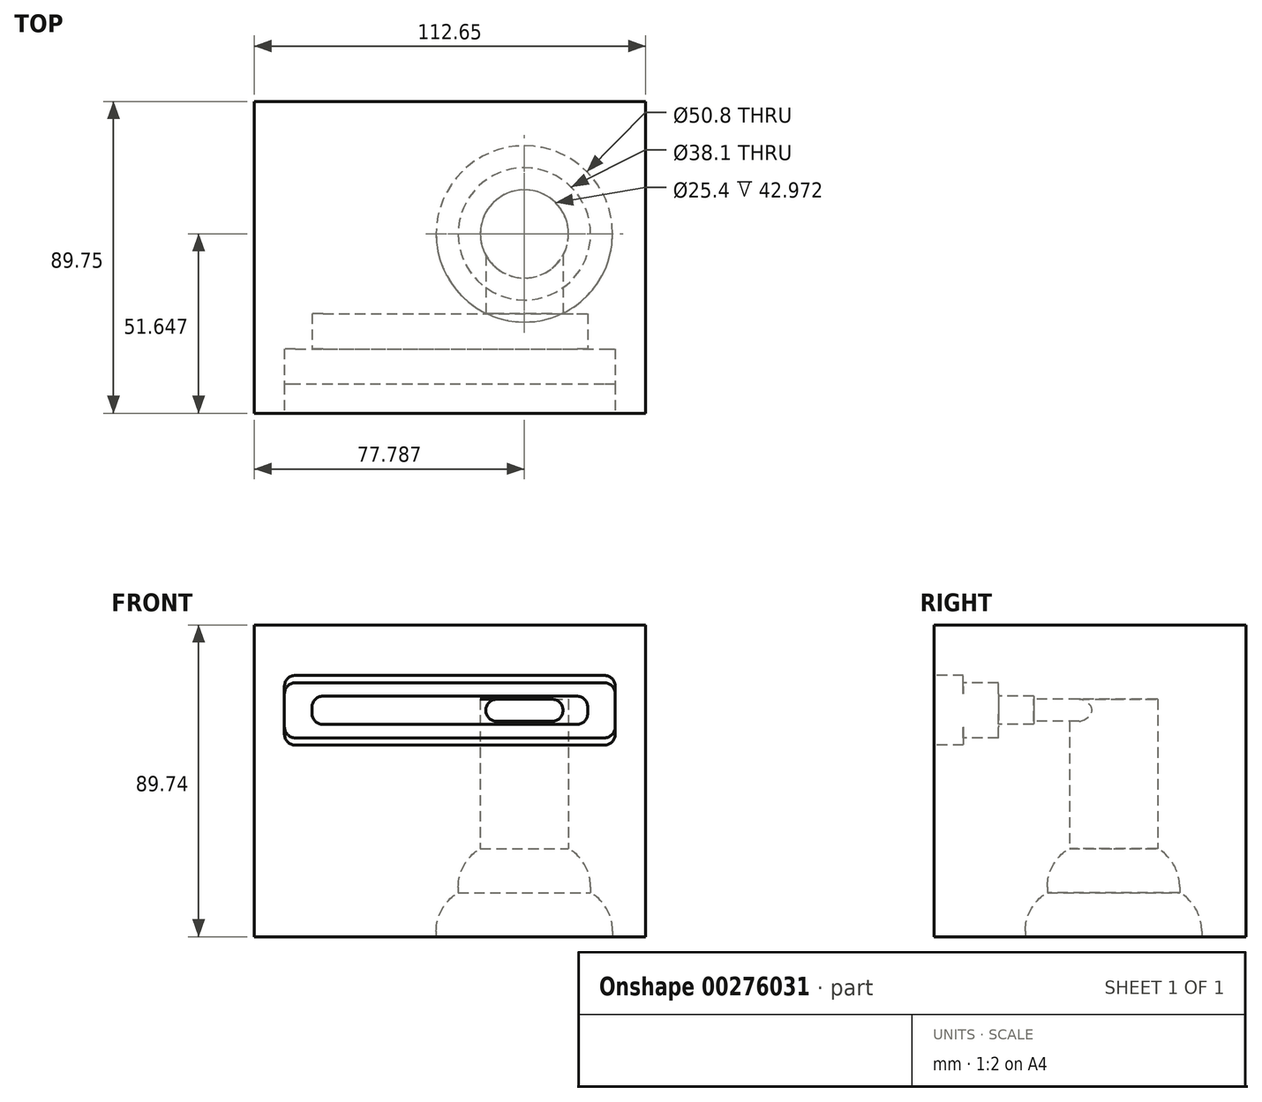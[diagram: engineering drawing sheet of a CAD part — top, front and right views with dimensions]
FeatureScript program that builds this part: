
annotation { "Feature Type Name" : "Feature", "Feature Type Description" : "" }
export const myFeature = defineFeature(function(context is Context, id is Id, definition is map)
    precondition{}
    {
        {
            var Q0;
            Q0=qCreatedBy(makeId("Right.planeOp"),FACE);
            var sketch = newSketch(context, id + "F0", { "sketchPlane" : qUnion([Q0])});
            skLineSegment(sketch, "E0.bottom", {"start": v(-45.07, 37.37) * mm, "end": v(44.68, 37.37) * mm});
            skLineSegment(sketch, "E0.top", {"start": v(-45.07, -52.37) * mm, "end": v(44.68, -52.37) * mm});
            skLineSegment(sketch, "E0.left", {"start": v(-45.07, 37.37) * mm, "end": v(-45.07, -52.37) * mm});
            skLineSegment(sketch, "E0.right", {"start": v(44.68, 37.37) * mm, "end": v(44.68, -52.37) * mm});
            skSolve(sketch);
        }
        {
            var Q0;
            Q0 = qSketchRegion(id + "F0", true);
            extrude(context, id + "F1", {"entities" : qUnion([Q0]), "depth" : 112.65 * mm});
        }
        {
            var Q0;
            Q0=makeQuery(id+"F1.opExtrude","SWEPT_FACE",FACE,{"disambiguationData":[OSD([sQuery(id+"F0.wireOp",EDGE,"E0.left")])]});
            var sketch = newSketch(context, id + "F2", { "sketchPlane" : qUnion([Q0])});
            skLineSegment(sketch, "E1.0", {"start": v(100.77, 22.88) * mm, "end": v(11.87, 22.88) * mm});
            skLineSegment(sketch, "E2.0", {"start": v(100.77, 2.77) * mm, "end": v(11.87, 2.77) * mm});
            skLineSegment(sketch, "E3.0", {"start": v(8.7, 19.7) * mm, "end": v(8.7, 5.94) * mm});
            skLineSegment(sketch, "E4.0", {"start": v(103.95, 19.7) * mm, "end": v(103.95, 5.94) * mm});
            skLineSegment(sketch, "E5.3", {"start": v(-47.62, -100) * mm, "end": v(160.27, -100) * mm});
            skPoint(sketch, "E6.orphan", {"position": v(56.32, 37.37) * mm});
            skPoint(sketch, "E7.orphan", {"position": v(0, 12.83) * mm});
            skPoint(sketch, "E8.orphan", {"position": v(0, -7.5) * mm});
            skPoint(sketch, "E9.orphan", {"position": v(56.32, -52.37) * mm});
            skPoint(sketch, "E10.end.orphan", {"position": v(112.65, -7.5) * mm});
            skPoint(sketch, "E11.visualSharp", {"position": v(8.7, 22.88) * mm});
            skArc(sketch, "E11.filletArc", {"start": v(11.87, 22.88) * mm, "mid": v(9.63, 21.95) * mm, "end": v(8.7, 19.7) * mm});
            skPoint(sketch, "E12.visualSharp", {"position": v(8.7, 2.77) * mm});
            skArc(sketch, "E12.filletArc", {"start": v(8.7, 5.94) * mm, "mid": v(9.63, 3.7) * mm, "end": v(11.87, 2.77) * mm});
            skPoint(sketch, "E13.visualSharp", {"position": v(103.95, 2.77) * mm});
            skArc(sketch, "E13.filletArc", {"start": v(100.77, 2.77) * mm, "mid": v(103.02, 3.7) * mm, "end": v(103.95, 5.94) * mm});
            skPoint(sketch, "E14.visualSharp", {"position": v(103.95, 22.88) * mm});
            skArc(sketch, "E14.filletArc", {"start": v(103.95, 19.7) * mm, "mid": v(103.02, 21.95) * mm, "end": v(100.77, 22.88) * mm});
            skSolve(sketch);
        }
        {
            var Q0;
            Q0 = qSketchRegion(id + "F2", true);
            extrude(context, id + "F3", {"entities" : qUnion([Q0]), "operationType" : NewBodyOperationType.REMOVE, "oppositeDirection" : true, "depth" : 8.38 * mm});
        }
        {
            var Q0;
            Q0=makeQuery(id+"F3.boolean.opBoolean","COPY",FACE,{"derivedFrom":makeQuery(id+"F3.opExtrude","CAP_FACE",FACE,{"disambiguationData":[OSD([sQuery(id+"F2.wireOp",EDGE,"E1.0"),sQuery(id+"F2.wireOp",EDGE,"E2.0"),sQuery(id+"F2.wireOp",EDGE,"E3.0"),sQuery(id+"F2.wireOp",EDGE,"E4.0"),sQuery(id+"F2.wireOp",EDGE,"E11.filletArc"),sQuery(id+"F2.wireOp",EDGE,"E12.filletArc"),sQuery(id+"F2.wireOp",EDGE,"E13.filletArc"),sQuery(id+"F2.wireOp",EDGE,"E14.filletArc")])],"isStart":false})});
            var sketch = newSketch(context, id + "F4", { "sketchPlane" : qUnion([Q0])});
            skLineSegment(sketch, "E15.0", {"start": v(11.87, 4.89) * mm, "end": v(100.77, 4.89) * mm});
            skLineSegment(sketch, "E16.0", {"start": v(11.87, 20.76) * mm, "end": v(100.77, 20.76) * mm});
            skLineSegment(sketch, "E17", {"start": v(8.7, 17.59) * mm, "end": v(8.7, 8.06) * mm});
            skLineSegment(sketch, "E18", {"start": v(103.95, 17.59) * mm, "end": v(103.95, 8.06) * mm});
            skPoint(sketch, "E19.visualSharp", {"position": v(103.95, 20.76) * mm});
            skArc(sketch, "E19.filletArc", {"start": v(103.95, 17.59) * mm, "mid": v(103.02, 19.83) * mm, "end": v(100.77, 20.76) * mm});
            skPoint(sketch, "E20.visualSharp", {"position": v(103.95, 4.89) * mm});
            skArc(sketch, "E20.filletArc", {"start": v(100.77, 4.89) * mm, "mid": v(103.02, 5.82) * mm, "end": v(103.95, 8.06) * mm});
            skPoint(sketch, "E21.visualSharp", {"position": v(8.7, 4.89) * mm});
            skArc(sketch, "E21.filletArc", {"start": v(8.7, 8.06) * mm, "mid": v(9.63, 5.82) * mm, "end": v(11.87, 4.89) * mm});
            skPoint(sketch, "E22.visualSharp", {"position": v(8.7, 20.76) * mm});
            skArc(sketch, "E22.filletArc", {"start": v(11.87, 20.76) * mm, "mid": v(9.63, 19.83) * mm, "end": v(8.7, 17.59) * mm});
            skSolve(sketch);
        }
        {
            var Q0;
            Q0=makeQuery(id+"F4.imprint","IMPRINT",FACE,{"disambiguationData":[TD([[makeQuery(id+"F4.imprint","IMPRINT",EDGE,{"derivedFrom":sQuery(id+"F4.wireOp",EDGE,"E15.0")}),1.0]])]});
            extrude(context, id + "F5", {"entities" : qUnion([Q0]), "operationType" : NewBodyOperationType.REMOVE, "oppositeDirection" : true, "depth" : 10.16 * mm});
        }
        {
            var Q0;
            Q0=makeQuery(id+"F5.boolean.opBoolean","COPY",FACE,{"derivedFrom":makeQuery(id+"F5.opExtrude","CAP_FACE",FACE,{"disambiguationData":[OSD([sQuery(id+"F4.wireOp",EDGE,"E15.0"),sQuery(id+"F4.wireOp",EDGE,"E16.0"),sQuery(id+"F4.wireOp",EDGE,"E17"),sQuery(id+"F4.wireOp",EDGE,"E18"),sQuery(id+"F4.wireOp",EDGE,"E19.filletArc"),sQuery(id+"F4.wireOp",EDGE,"E20.filletArc"),sQuery(id+"F4.wireOp",EDGE,"E21.filletArc"),sQuery(id+"F4.wireOp",EDGE,"E22.filletArc")])],"isStart":false})});
            var sketch = newSketch(context, id + "F6", { "sketchPlane" : qUnion([Q0])});
            skLineSegment(sketch, "E23.0", {"start": v(19.81, 8.76) * mm, "end": v(92.84, 8.76) * mm});
            skLineSegment(sketch, "E24.0", {"start": v(19.81, 16.89) * mm, "end": v(92.84, 16.89) * mm});
            skLineSegment(sketch, "E25.0", {"start": v(16.64, 13.71) * mm, "end": v(16.64, 11.94) * mm});
            skLineSegment(sketch, "E26.0", {"start": v(96.01, 13.71) * mm, "end": v(96.01, 11.94) * mm});
            skPoint(sketch, "E27.orphan", {"position": v(8.7, 12.83) * mm});
            skPoint(sketch, "E28.orphan", {"position": v(56.32, 20.76) * mm});
            skPoint(sketch, "E29.orphan", {"position": v(103.95, 12.83) * mm});
            skPoint(sketch, "E30.visualSharp", {"position": v(16.64, 16.89) * mm});
            skArc(sketch, "E30.filletArc", {"start": v(19.81, 16.89) * mm, "mid": v(17.57, 15.96) * mm, "end": v(16.64, 13.71) * mm});
            skPoint(sketch, "E31.visualSharp", {"position": v(16.64, 8.76) * mm});
            skArc(sketch, "E31.filletArc", {"start": v(16.64, 11.94) * mm, "mid": v(17.57, 9.7) * mm, "end": v(19.81, 8.76) * mm});
            skPoint(sketch, "E32.visualSharp", {"position": v(96.01, 16.89) * mm});
            skArc(sketch, "E32.filletArc", {"start": v(96.01, 13.71) * mm, "mid": v(95.08, 15.96) * mm, "end": v(92.84, 16.89) * mm});
            skPoint(sketch, "E33.visualSharp", {"position": v(96.01, 8.76) * mm});
            skArc(sketch, "E33.filletArc", {"start": v(92.84, 8.76) * mm, "mid": v(95.08, 9.7) * mm, "end": v(96.01, 11.94) * mm});
            skSolve(sketch);
        }
        {
            var Q0;
            Q0=makeQuery(id+"F6.imprint","IMPRINT",FACE,{"disambiguationData":[TD([[makeQuery(id+"F6.imprint","IMPRINT",EDGE,{"derivedFrom":sQuery(id+"F6.wireOp",EDGE,"E23.0")}),1.0]])]});
            extrude(context, id + "F7", {"entities" : qUnion([Q0]), "operationType" : NewBodyOperationType.REMOVE, "oppositeDirection" : true, "depth" : 10.16 * mm});
        }
        {
            var Q0;
            Q0=makeQuery(id+"F7.boolean.opBoolean","COPY",FACE,{"derivedFrom":makeQuery(id+"F7.opExtrude","CAP_FACE",FACE,{"disambiguationData":[OSD([sQuery(id+"F6.wireOp",EDGE,"E23.0"),sQuery(id+"F6.wireOp",EDGE,"E24.0"),sQuery(id+"F6.wireOp",EDGE,"E25.0"),sQuery(id+"F6.wireOp",EDGE,"E26.0"),sQuery(id+"F6.wireOp",EDGE,"E30.filletArc"),sQuery(id+"F6.wireOp",EDGE,"E31.filletArc"),sQuery(id+"F6.wireOp",EDGE,"E32.filletArc"),sQuery(id+"F6.wireOp",EDGE,"E33.filletArc")])],"isStart":false})});
            var sketch = newSketch(context, id + "F8", { "sketchPlane" : qUnion([Q0])});
            skPoint(sketch, "E34.endSnap0", {"position": v(96.01, 12.83) * mm});
            skLineSegment(sketch, "E35.0", {"start": v(85.72, 16) * mm, "end": v(69.85, 16) * mm});
            skLineSegment(sketch, "E36.0", {"start": v(85.72, 9.65) * mm, "end": v(69.85, 9.65) * mm});
            skLineSegment(sketch, "E37", {"start": v(66.67, 12.83) * mm, "end": v(66.67, 12.83) * mm});
            skLineSegment(sketch, "E38", {"start": v(88.9, 12.83) * mm, "end": v(88.9, 12.83) * mm});
            skPoint(sketch, "E39.visualSharp", {"position": v(66.67, 16) * mm});
            skArc(sketch, "E39.filletArc", {"start": v(69.85, 16) * mm, "mid": v(67.6, 15.07) * mm, "end": v(66.67, 12.83) * mm});
            skPoint(sketch, "E40.visualSharp", {"position": v(66.67, 9.65) * mm});
            skArc(sketch, "E40.filletArc", {"start": v(66.67, 12.83) * mm, "mid": v(67.6, 10.58) * mm, "end": v(69.85, 9.65) * mm});
            skPoint(sketch, "E41.visualSharp", {"position": v(88.9, 16) * mm});
            skArc(sketch, "E41.filletArc", {"start": v(88.9, 12.83) * mm, "mid": v(87.97, 15.07) * mm, "end": v(85.72, 16) * mm});
            skPoint(sketch, "E42.visualSharp", {"position": v(88.9, 9.65) * mm});
            skArc(sketch, "E42.filletArc", {"start": v(85.72, 9.65) * mm, "mid": v(87.97, 10.58) * mm, "end": v(88.9, 12.83) * mm});
            skSolve(sketch);
        }
        {
            var Q0;
            Q0=makeQuery(id+"F8.imprint","IMPRINT",FACE,{"disambiguationData":[TD([[makeQuery(id+"F8.imprint","IMPRINT",EDGE,{"derivedFrom":sQuery(id+"F8.wireOp",EDGE,"E35.0")}),1.0]])]});
            extrude(context, id + "F9", {"entities" : qUnion([Q0]), "operationType" : NewBodyOperationType.REMOVE, "oppositeDirection" : true, "depth" : 25.4 * mm});
        }
        {
            var Q0;
            Q0=makeQuery(id+"F1.opExtrude","SWEPT_FACE",FACE,{"disambiguationData":[OSD([sQuery(id+"F0.wireOp",EDGE,"E0.top")])]});
            var sketch = newSketch(context, id + "F10", { "sketchPlane" : qUnion([Q0])});
            skCircle(sketch, "E43", {"center": v(77.79, -6.58) * mm, "radius": 25.4 * mm});
            skSolve(sketch);
        }
        {
            var Q0;
            Q0 = qSketchRegion(id + "F10", true);
            extrude(context, id + "F11", {"entities" : qUnion([Q0]), "operationType" : NewBodyOperationType.REMOVE, "oppositeDirection" : true, "depth" : 12.7 * mm});
        }
        {
            var Q0;
            Q0=makeQuery(id+"F11.boolean.opBoolean","COPY",FACE,{"derivedFrom":makeQuery(id+"F11.opExtrude","CAP_FACE",FACE,{"disambiguationData":[OSD([sQuery(id+"F10.wireOp",EDGE,"E43")])],"isStart":false})});
            var sketch = newSketch(context, id + "F12", { "sketchPlane" : qUnion([Q0])});
            skCircle(sketch, "E44", {"center": v(77.79, -6.58) * mm, "radius": 19.05 * mm});
            skSolve(sketch);
        }
        {
            var Q0;
            Q0=makeQuery(id+"F12.imprint","IMPRINT",FACE,{"disambiguationData":[TD([[makeQuery(id+"F12.imprint","IMPRINT",EDGE,{"derivedFrom":sQuery(id+"F12.wireOp",EDGE,"E44")}),1.0]])]});
            extrude(context, id + "F13", {"entities" : qUnion([Q0]), "operationType" : NewBodyOperationType.REMOVE, "oppositeDirection" : true, "depth" : 12.7 * mm});
        }
        {
            var Q0;
            Q0=makeQuery(id+"F13.boolean.opBoolean","COPY",FACE,{"derivedFrom":makeQuery(id+"F13.opExtrude","CAP_FACE",FACE,{"disambiguationData":[OSD([sQuery(id+"F12.wireOp",EDGE,"E44")])],"isStart":false})});
            var sketch = newSketch(context, id + "F14", { "sketchPlane" : qUnion([Q0])});
            skCircle(sketch, "E45", {"center": v(77.79, -6.58) * mm, "radius": 12.7 * mm});
            skSolve(sketch);
        }
        {
            var Q0;
            Q0=makeQuery(id+"F14.imprint","IMPRINT",FACE,{"disambiguationData":[TD([[makeQuery(id+"F14.imprint","IMPRINT",EDGE,{"derivedFrom":sQuery(id+"F14.wireOp",EDGE,"E45")}),1.0]])]});
            extrude(context, id + "F15", {"entities" : qUnion([Q0]), "operationType" : NewBodyOperationType.REMOVE, "oppositeDirection" : true, "depth" : 42.97 * mm});
        }
        {
            var Q0;
            Q0=makeQuery(id+"F11.boolean.opBoolean","COPY",EDGE,{"derivedFrom":makeQuery(id+"F11.opExtrude","CAP_EDGE",EDGE,{"disambiguationData":[OSD([sQuery(id+"F10.wireOp",EDGE,"E43")])],"isStart":false})});
            var Q1;
            Q1=makeQuery(id+"F13.boolean.opBoolean","COPY",EDGE,{"derivedFrom":makeQuery(id+"F13.opExtrude","CAP_EDGE",EDGE,{"disambiguationData":[OSD([sQuery(id+"F12.wireOp",EDGE,"E44")])],"isStart":false})});
            fillet(context, id + "F16", {"entities" : qUnion([Q0, Q1]), "radius" : 12.9 * mm, "tangentPropagation" : true, "allowEdgeOverflow" : false});
        }
    });
